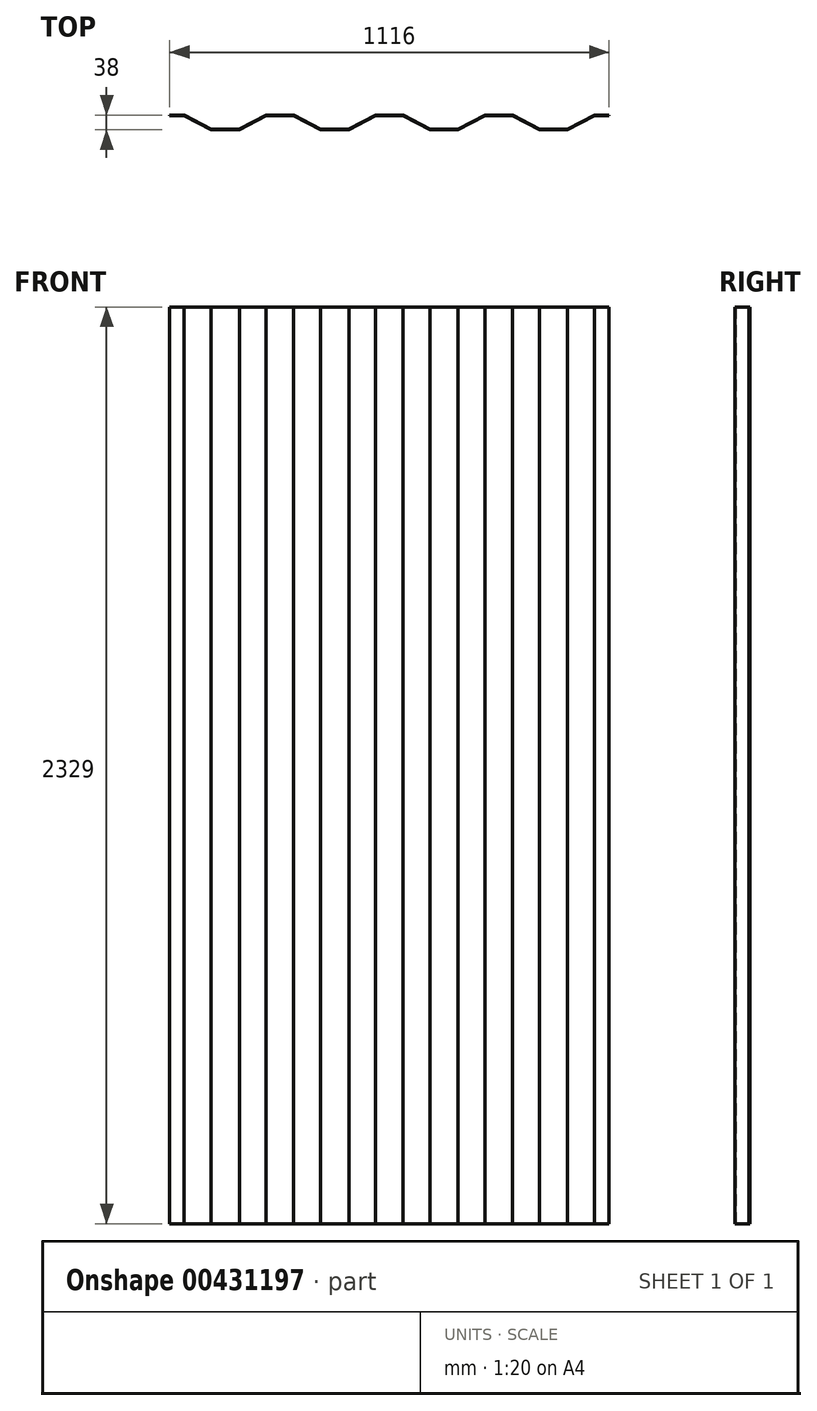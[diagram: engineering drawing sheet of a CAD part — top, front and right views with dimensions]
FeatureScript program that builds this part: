
annotation { "Feature Type Name" : "Feature", "Feature Type Description" : "" }
export const myFeature = defineFeature(function(context is Context, id is Id, definition is map)
    precondition{}
    {
        {
            var Q0;
            Q0=qCreatedBy(makeId("Top.planeOp"),FACE);
            var sketch = newSketch(context, id + "F0", { "sketchPlane" : qUnion([Q0])});
            skPoint(sketch, "E0", {"position": v(0, -36) * mm});
            skLineSegment(sketch, "E1", {"start": v(0, 0) * mm, "end": v(37, 0) * mm});
            skLineSegment(sketch, "E2", {"start": v(37, 0) * mm, "end": v(105, -36) * mm});
            skLineSegment(sketch, "E3", {"start": v(177, -36) * mm, "end": v(105, -36) * mm});
            skLineSegment(sketch, "E4", {"start": v(177, -36) * mm, "end": v(245, 0) * mm});
            skLineSegment(sketch, "E5", {"start": v(245, 0) * mm, "end": v(315, 0) * mm});
            skLineSegment(sketch, "E6.0", {"start": v(0, 2) * mm, "end": v(37.5, 2) * mm});
            skLineSegment(sketch, "E7", {"start": v(0, 0) * mm, "end": v(0, 2) * mm});
            skLineSegment(sketch, "E8.0", {"start": v(37.5, 2) * mm, "end": v(105.5, -34) * mm});
            skLineSegment(sketch, "E9.0", {"start": v(176.5, -34) * mm, "end": v(105.5, -34) * mm});
            skLineSegment(sketch, "E10.0", {"start": v(176.5, -34) * mm, "end": v(244.5, 2) * mm});
            skLineSegment(sketch, "E11.0", {"start": v(244.5, 2) * mm, "end": v(315.5, 2) * mm});
            skLineSegment(sketch, "E12", {"start": v(315, 0) * mm, "end": v(383, -36) * mm});
            skLineSegment(sketch, "E13", {"start": v(455, -36) * mm, "end": v(383, -36) * mm});
            skLineSegment(sketch, "E14", {"start": v(455, -36) * mm, "end": v(523, 0) * mm});
            skLineSegment(sketch, "E15", {"start": v(523, 0) * mm, "end": v(593, 0) * mm});
            skLineSegment(sketch, "E16.0", {"start": v(315.5, 2) * mm, "end": v(383.5, -34) * mm});
            skLineSegment(sketch, "E17.0", {"start": v(454.5, -34) * mm, "end": v(383.5, -34) * mm});
            skLineSegment(sketch, "E18.0", {"start": v(454.5, -34) * mm, "end": v(522.5, 2) * mm});
            skLineSegment(sketch, "E19.0", {"start": v(522.5, 2) * mm, "end": v(593.5, 2) * mm});
            skLineSegment(sketch, "E20", {"start": v(593, 0) * mm, "end": v(661, -36) * mm});
            skLineSegment(sketch, "E21", {"start": v(733, -36) * mm, "end": v(661, -36) * mm});
            skLineSegment(sketch, "E22", {"start": v(733, -36) * mm, "end": v(801, 0) * mm});
            skLineSegment(sketch, "E23", {"start": v(801, 0) * mm, "end": v(871, 0) * mm});
            skLineSegment(sketch, "E24.0", {"start": v(593.5, 2) * mm, "end": v(661.5, -34) * mm});
            skLineSegment(sketch, "E25.0", {"start": v(732.5, -34) * mm, "end": v(661.5, -34) * mm});
            skLineSegment(sketch, "E26.0", {"start": v(732.5, -34) * mm, "end": v(800.5, 2) * mm});
            skLineSegment(sketch, "E27.0", {"start": v(800.5, 2) * mm, "end": v(871.5, 2) * mm});
            skLineSegment(sketch, "E28", {"start": v(871, 0) * mm, "end": v(939, -36) * mm});
            skLineSegment(sketch, "E29", {"start": v(1011, -36) * mm, "end": v(939, -36) * mm});
            skLineSegment(sketch, "E30", {"start": v(1011, -36) * mm, "end": v(1079, 0) * mm});
            skLineSegment(sketch, "E31", {"start": v(1079, 0) * mm, "end": v(1116, 0) * mm});
            skLineSegment(sketch, "E32.0", {"start": v(871.5, 2) * mm, "end": v(939.5, -34) * mm});
            skLineSegment(sketch, "E33.0", {"start": v(1010.5, -34) * mm, "end": v(939.5, -34) * mm});
            skLineSegment(sketch, "E34.0", {"start": v(1010.5, -34) * mm, "end": v(1078.5, 2) * mm});
            skLineSegment(sketch, "E35", {"start": v(1078.5, 2) * mm, "end": v(1116, 2) * mm});
            skLineSegment(sketch, "E36", {"start": v(1116, 2) * mm, "end": v(1116, 0) * mm});
            skSolve(sketch);
        }
        {
            var Q0;
            Q0 = qSketchRegion(id + "F0", true);
            extrude(context, id + "F1", {"entities" : qUnion([Q0]), "depth" : 2329 * mm});
        }
    });
